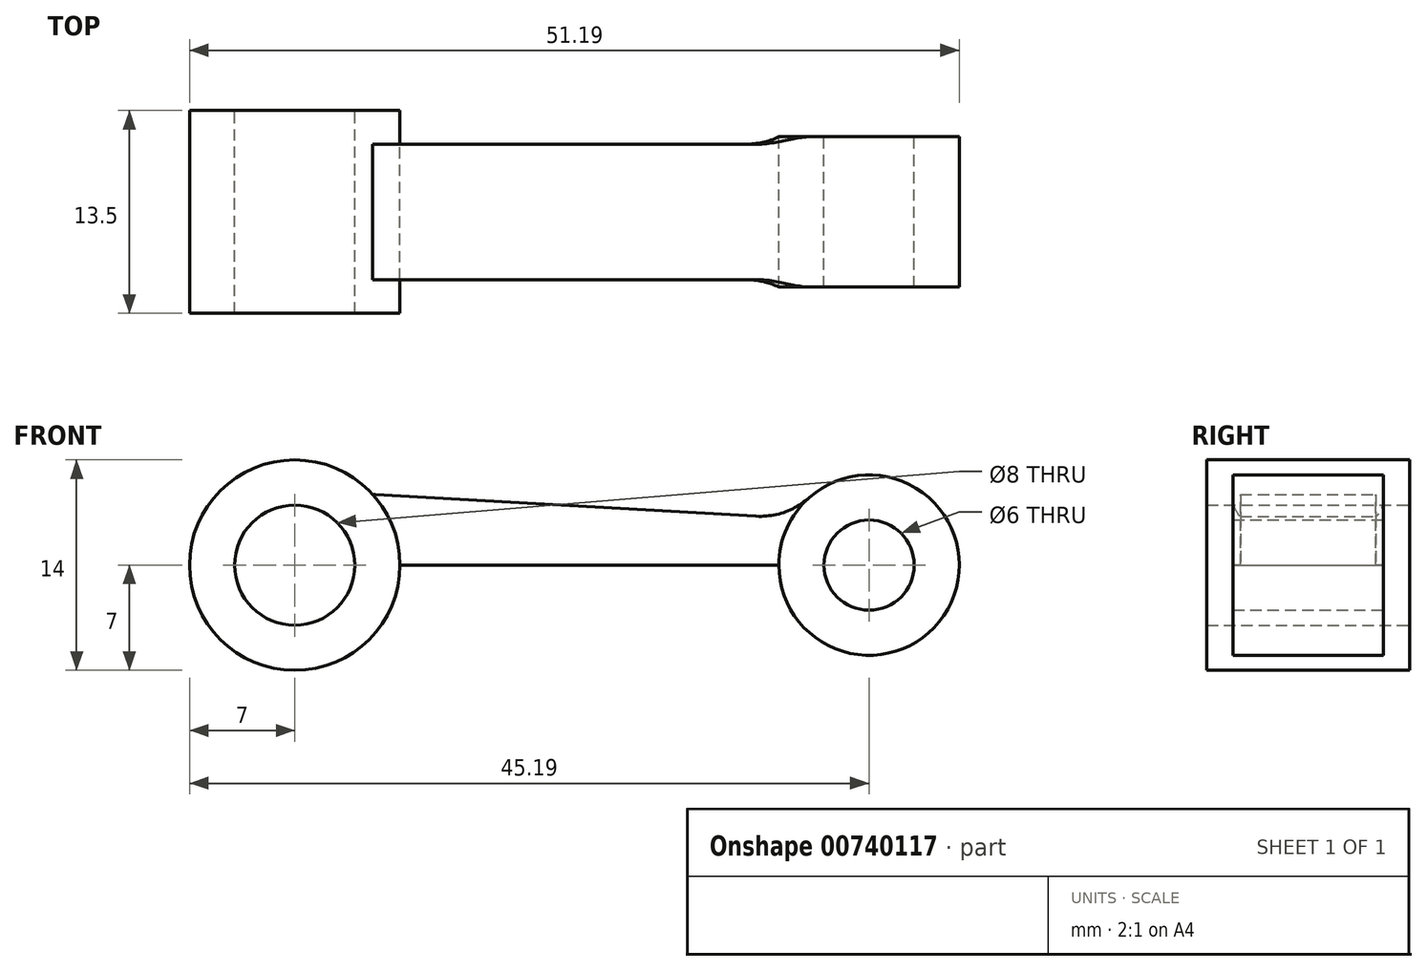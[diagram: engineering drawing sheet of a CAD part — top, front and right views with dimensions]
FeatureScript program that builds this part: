
annotation { "Feature Type Name" : "Feature", "Feature Type Description" : "" }
export const myFeature = defineFeature(function(context is Context, id is Id, definition is map)
    precondition{}
    {
        {
            var Q0;
            Q0=qCreatedBy(makeId("Front.planeOp"),FACE);
            var sketch = newSketch(context, id + "F0", { "sketchPlane" : qUnion([Q0])});
            skCircle(sketch, "E0", {"center": v(0, 0) * mm, "radius": 4 * mm});
            skCircle(sketch, "E1", {"center": v(0, 0) * mm, "radius": 7 * mm});
            skSolve(sketch);
        }
        {
            var Q0;
            Q0 = qSketchRegion(id + "F0", true);
            extrude(context, id + "F1", {"entities" : qUnion([Q0]), "depth" : 13.5 * mm, "offsetDistance" : 25 * mm, "symmetric" : true});
        }
        {
            var Q0;
            Q0=qCreatedBy(makeId("Front.planeOp"),FACE);
            var sketch = newSketch(context, id + "F2", { "sketchPlane" : qUnion([Q0])});
            skCircle(sketch, "E2.0", {"center": v(0, 0) * mm, "radius": 7 * mm});
            skLineSegment(sketch, "E3", {"start": v(5.19, 0) * mm, "end": v(5.19, 4.7) * mm});
            skLineSegment(sketch, "E4", {"start": v(5.19, 4.7) * mm, "end": v(35.19, 3) * mm});
            skLineSegment(sketch, "E5", {"start": v(35.19, 3) * mm, "end": v(35.19, 0) * mm});
            skLineSegment(sketch, "E6", {"start": v(35.19, 0) * mm, "end": v(5.19, 0) * mm});
            skLineSegment(sketch, "E7.MirrorCS", {"start": v(5.72, 9.37) * mm, "end": v(5.19, 4.7) * mm});
            skLineSegment(sketch, "E8.MirrorCS", {"start": v(35.19, 3) * mm, "end": v(35.53, 5.98) * mm});
            skSolve(sketch);
        }
        {
            var Q0;
            {var subQ0=sQuery(id+"F2.wireOp",EDGE,"E4");Q0=makeQuery(id+"F2.imprint","IMPRINT",FACE,{"disambiguationData":[TD([[makeQuery(id+"F2.imprint","IMPRINT",EDGE,{"derivedFrom":subQ0}),-1.0]])]});}
            var Q1;
            {var subQ0=sQuery(id+"FEcYFd18Gh4tjGo_1.1.F2.wireOp",EDGE,"E4");Q1=makeQuery(id+"FEcYFd18Gh4tjGo_1.1.F2.imprint","IMPRINT",FACE,{"disambiguationData":[TD([[makeQuery(id+"FEcYFd18Gh4tjGo_1.1.F2.imprint","IMPRINT",EDGE,{"derivedFrom":subQ0}),-1.0]])]});}
            extrude(context, id + "F3", {"entities" : qUnion([Q0, Q1]), "operationType" : NewBodyOperationType.ADD, "depth" : 9 * mm, "offsetDistance" : 25 * mm, "symmetric" : true});
        }
        {
            var Q0;
            Q0=makeQuery(id+"F3.opExtrude","SWEPT_EDGE",EDGE,{"disambiguationData":[OSD([sQuery(id+"F2.wireOp",EDGE,"E2.0"),sQuery(id+"F2.wireOp",EDGE,"E3"),sQuery(id+"F2.wireOp",EDGE,"E4")])]});
            var Q1;
            Q1=makeQuery(id+"F3.opExtrude","SWEPT_EDGE",EDGE,{"disambiguationData":[OSD([sQuery(id+"FEcYFd18Gh4tjGo_1.1.F2.wireOp",EDGE,"E2.0"),sQuery(id+"FEcYFd18Gh4tjGo_1.1.F2.wireOp",EDGE,"E3"),sQuery(id+"FEcYFd18Gh4tjGo_1.1.F2.wireOp",EDGE,"E4")])]});
            var Q2;
            Q2=makeQuery(id+"F3.boolean.opBoolean","MERGE",EDGE,{"derivedFrom":[makeQuery(id+"F3.opExtrude","CAP_EDGE",EDGE,{"disambiguationData":[OSD([sQuery(id+"F2.wireOp",EDGE,"E2.0")])],"isStart":false}),makeQuery(id+"F3.opExtrude","CAP_EDGE",EDGE,{"disambiguationData":[OSD([sQuery(id+"FEcYFd18Gh4tjGo_1.1.F2.wireOp",EDGE,"E2.0")])],"isStart":false})]});
            var Q3;
            Q3=makeQuery(id+"F3.boolean.opBoolean","MERGE",EDGE,{"derivedFrom":[makeQuery(id+"F3.opExtrude","CAP_EDGE",EDGE,{"disambiguationData":[OSD([sQuery(id+"F2.wireOp",EDGE,"E2.0")])],"isStart":true}),makeQuery(id+"F3.opExtrude","CAP_EDGE",EDGE,{"disambiguationData":[OSD([sQuery(id+"FEcYFd18Gh4tjGo_1.1.F2.wireOp",EDGE,"E2.0")])],"isStart":true})]});
            fillet(context, id + "F4", {"entities" : qUnion([Q0, Q1, Q2, Q3]), "radius" : 5 * mm, "tangentPropagation" : true, "allowEdgeOverflow" : false});
        }
        {
            var Q0;
            Q0=qCreatedBy(makeId("Front.planeOp"),FACE);
            var sketch = newSketch(context, id + "F5", { "sketchPlane" : qUnion([Q0])});
            skCircle(sketch, "E9", {"center": v(38.19, 0) * mm, "radius": 3 * mm});
            skCircle(sketch, "E10", {"center": v(38.19, 0) * mm, "radius": 6 * mm});
            skSolve(sketch);
        }
        {
            var Q0;
            Q0=makeQuery(id+"F5.imprint","IMPRINT",FACE,{"disambiguationData":[TD([[makeQuery(id+"F5.imprint","IMPRINT",EDGE,{"derivedFrom":sQuery(id+"F5.wireOp",EDGE,"E9")}),-1.0]])]});
            extrude(context, id + "F6", {"entities" : qUnion([Q0]), "operationType" : NewBodyOperationType.ADD, "depth" : 10 * mm, "offsetDistance" : 25 * mm, "symmetric" : true});
        }
        {
            var Q0;
            Q0=makeQuery(id+"F6.boolean.opBoolean","INTERSECT",EDGE,{"derivedFrom":[makeQuery(id+"F3.opExtrude","SWEPT_FACE",FACE,{"disambiguationData":[OSD([sQuery(id+"F2.wireOp",EDGE,"E4")])]}),makeQuery(id+"F6.opExtrude","SWEPT_FACE",FACE,{"disambiguationData":[OSD([sQuery(id+"F5.wireOp",EDGE,"E10")])]})]});
            var Q1;
            Q1=makeQuery(id+"F6.boolean.opBoolean","INTERSECT",EDGE,{"derivedFrom":[makeQuery(id+"F3.boolean.opBoolean","MERGE",FACE,{"derivedFrom":[makeQuery(id+"F3.opExtrude","CAP_FACE",FACE,{"disambiguationData":[OSD([sQuery(id+"F2.wireOp",EDGE,"E2.0"),sQuery(id+"F2.wireOp",EDGE,"E4"),sQuery(id+"F2.wireOp",EDGE,"E5"),sQuery(id+"F2.wireOp",EDGE,"E6")])],"isStart":true}),makeQuery(id+"F3.opExtrude","CAP_FACE",FACE,{"disambiguationData":[OSD([sQuery(id+"FEcYFd18Gh4tjGo_1.1.F2.wireOp",EDGE,"E2.0"),sQuery(id+"FEcYFd18Gh4tjGo_1.1.F2.wireOp",EDGE,"E4"),sQuery(id+"FEcYFd18Gh4tjGo_1.1.F2.wireOp",EDGE,"E5"),sQuery(id+"FEcYFd18Gh4tjGo_1.1.F2.wireOp",EDGE,"E6")])],"isStart":true})]}),makeQuery(id+"F6.opExtrude","SWEPT_FACE",FACE,{"disambiguationData":[OSD([sQuery(id+"F5.wireOp",EDGE,"E10")])]})]});
            var Q2;
            Q2=makeQuery(id+"F6.boolean.opBoolean","INTERSECT",EDGE,{"derivedFrom":[makeQuery(id+"F3.opExtrude","SWEPT_FACE",FACE,{"disambiguationData":[OSD([sQuery(id+"FEcYFd18Gh4tjGo_1.1.F2.wireOp",EDGE,"E4")])]}),makeQuery(id+"F6.opExtrude","SWEPT_FACE",FACE,{"disambiguationData":[OSD([sQuery(id+"F5.wireOp",EDGE,"E10")])]})]});
            var Q3;
            Q3=makeQuery(id+"F6.boolean.opBoolean","INTERSECT",EDGE,{"derivedFrom":[makeQuery(id+"F3.boolean.opBoolean","MERGE",FACE,{"derivedFrom":[makeQuery(id+"F3.opExtrude","CAP_FACE",FACE,{"disambiguationData":[OSD([sQuery(id+"F2.wireOp",EDGE,"E2.0"),sQuery(id+"F2.wireOp",EDGE,"E4"),sQuery(id+"F2.wireOp",EDGE,"E5"),sQuery(id+"F2.wireOp",EDGE,"E6")])],"isStart":false}),makeQuery(id+"F3.opExtrude","CAP_FACE",FACE,{"disambiguationData":[OSD([sQuery(id+"FEcYFd18Gh4tjGo_1.1.F2.wireOp",EDGE,"E2.0"),sQuery(id+"FEcYFd18Gh4tjGo_1.1.F2.wireOp",EDGE,"E4"),sQuery(id+"FEcYFd18Gh4tjGo_1.1.F2.wireOp",EDGE,"E5"),sQuery(id+"FEcYFd18Gh4tjGo_1.1.F2.wireOp",EDGE,"E6")])],"isStart":false})]}),makeQuery(id+"F6.opExtrude","SWEPT_FACE",FACE,{"disambiguationData":[OSD([sQuery(id+"F5.wireOp",EDGE,"E10")])]})]});
            fillet(context, id + "F7", {"entities" : qUnion([Q0, Q1, Q2, Q3]), "radius" : 5 * mm, "tangentPropagation" : true, "allowEdgeOverflow" : false});
        }
    });
